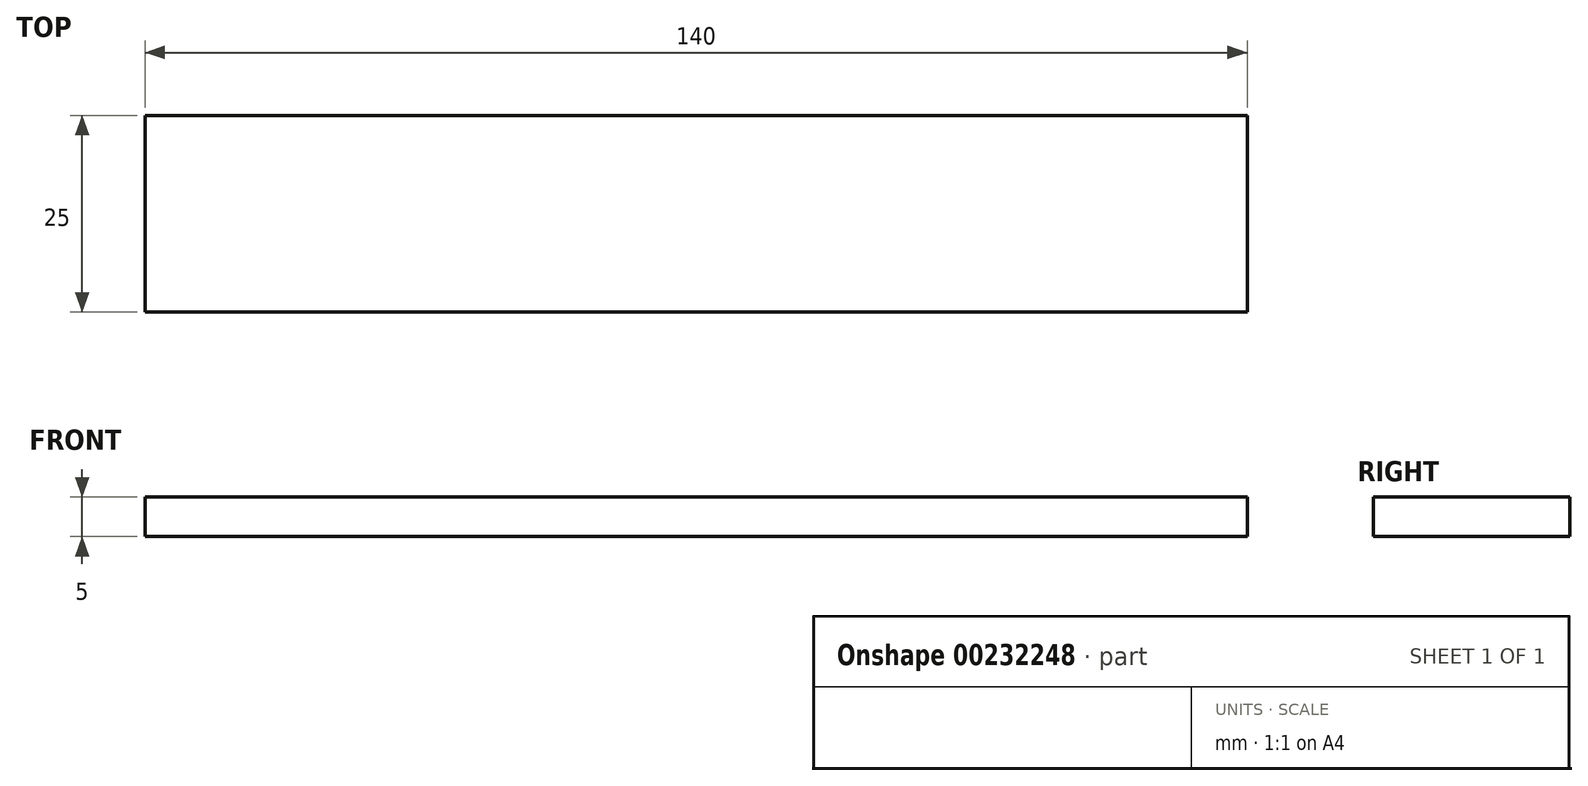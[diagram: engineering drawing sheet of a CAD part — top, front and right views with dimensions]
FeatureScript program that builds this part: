
annotation { "Feature Type Name" : "Feature", "Feature Type Description" : "" }
export const myFeature = defineFeature(function(context is Context, id is Id, definition is map)
    precondition{}
    {
        {
            var Q0;
            Q0=qCreatedBy(makeId("Top.planeOp"),FACE);
            var sketch = newSketch(context, id + "F0", { "sketchPlane" : qUnion([Q0])});
            skLineSegment(sketch, "E0.bottom", {"start": v(-64.95, -0.34) * mm, "end": v(75.05, -0.34) * mm});
            skLineSegment(sketch, "E0.top", {"start": v(-64.95, -25.34) * mm, "end": v(75.05, -25.34) * mm});
            skLineSegment(sketch, "E0.left", {"start": v(-64.95, -0.34) * mm, "end": v(-64.95, -25.34) * mm});
            skLineSegment(sketch, "E0.right", {"start": v(75.05, -0.34) * mm, "end": v(75.05, -25.34) * mm});
            skSolve(sketch);
        }
        {
            var Q0;
            Q0=makeQuery(id+"F0.imprint","IMPRINT",FACE,{"disambiguationData":[TD([[makeQuery(id+"F0.imprint","IMPRINT",EDGE,{"derivedFrom":sQuery(id+"F0.wireOp",EDGE,"E0.bottom")}),-1.0]])]});
            extrude(context, id + "F1", {"entities" : qUnion([Q0]), "depth" : 5 * mm});
        }
    });
